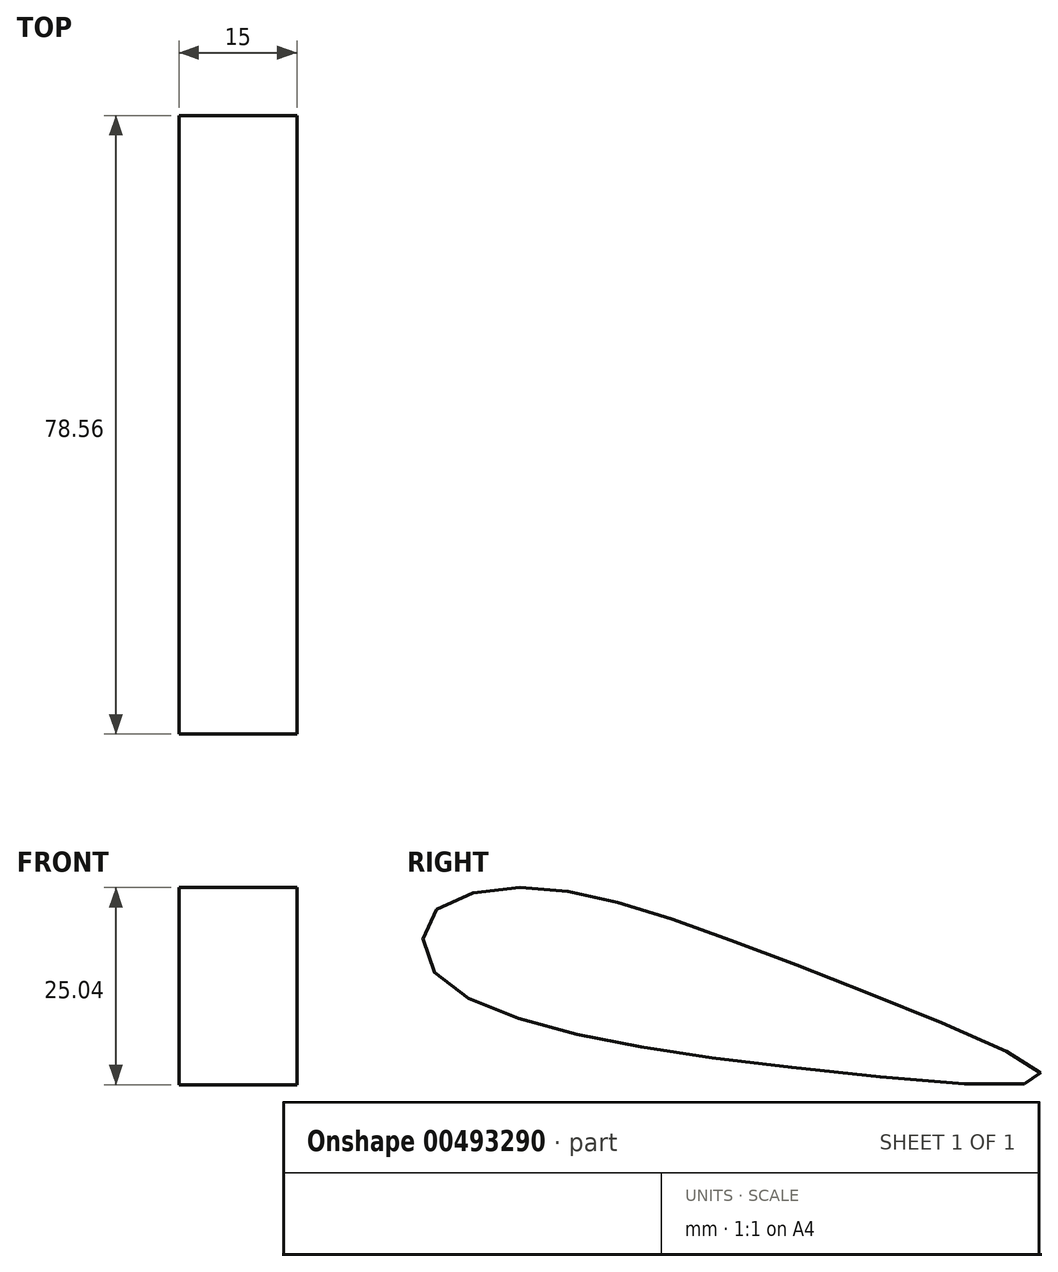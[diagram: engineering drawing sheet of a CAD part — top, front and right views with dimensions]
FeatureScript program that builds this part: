
annotation { "Feature Type Name" : "Feature", "Feature Type Description" : "" }
export const myFeature = defineFeature(function(context is Context, id is Id, definition is map)
    precondition{}
    {
        {
            var Q0;
            Q0=qCreatedBy(makeId("Right.planeOp"),FACE);
            var sketch = newSketch(context, id + "F0", { "sketchPlane" : qUnion([Q0])});
            skFitSpline(sketch, "E0", {"points": [v(-54.23, 11.21) * mm, v(-65.44, 7.78) * mm, v(-65.45, 0.9) * mm, v(-51.02, -6.42) * mm, v(-16.93, -11.95) * mm, v(11.95, -12.9) * mm, v(-7.15, -3.33) * mm, v(-37.46, 8.01) * mm, v(-54.23, 11.21) * mm]});
            skSolve(sketch);
        }
        {
            var Q0;
            Q0 = qSketchRegion(id + "F0", true);
            extrude(context, id + "F1", {"entities" : qUnion([Q0]), "depth" : 15 * mm});
        }
    });
